# Revit family: Mixer_Basin_Abey_Poco_FaceBased
name_source: partatom
category: Plumbing Fixtures
units: mm (PartAtom-declared; Revit-internal decimal feet)

## family parameters
Cut with Voids When Loaded = Yes
Host = Face
OmniClass Number = 23.31.11.00
OmniClass Title = Faucets
Part Type = Normal
Room Calculation Point = No
Round Connector Dimension = Use Diameter
Shared = No

## types (1)
- 6B1
    Assembly Code = C1030210
    CW Connection = Yes
    Default Elevation = 0 mm  [stored 0 ft]
    Description = Poco - Basin Mixer - Chrome
    HW Connection = Yes
    IfcExportAs = IfcValve
    IfcExportType = FAUCET
    Manufacturer = Abey
    ManufacturerOverallDepth = 155 mm  [stored 0.50853 ft]
    ManufacturerOverallHeight = 152 mm  [stored 0.498688 ft]
    ManufacturerOverallWidth = 38 mm  [stored 0.124672 ft]
    ManufacturerSpecCode = 6B1
    ManufacturerURLProductSpecific = https://www.abey.com.au
    Material = Metal_Abey_Chrome
    Model = 6B1
    ModifiedIssue = 20230628 $
    Type Comments = Chrome Finish
    URL = https://www.abey.com.au
    Uniclass2015Code = Pr_40_20_87_98
    Uniclass2015Title = Washbasin taps
    Uniclass2015Version = Products v1.28
    Vent Connection = No
    Waste Connection = No

note: [stored X ft] marks values corroborated as IEEE doubles in the binary element streams (Revit-internal decimal feet)

## geometry (parser evidence)
native form markers: Sweep x5
no freeform markers — native parametric forms only
